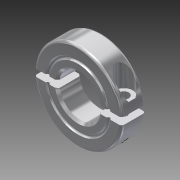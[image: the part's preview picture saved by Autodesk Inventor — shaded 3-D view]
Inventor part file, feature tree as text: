
AUTODESK INVENTOR PART (.ipt)
format: ipt  version: 2016 SP1 (Build 200210100, 210)  size: 259,584 bytes
history: native  units: in
note: dims shown in document units (in); Inventor stores cm internally (conversion verified against a paired STEP export)
features: thread x2, imported_body x2, other x1
ambient origin geometry x8: Origin, YZ Plane, XZ Plane, XY Plane, X Axis, Y Axis, Z Axis, Center Point
bodies: Solid1 (feature_tree), Solid2 (feature_tree)
feature tree (5):
  other  "ENSP20-6-A1"
  thread  "Thread1"  [1 undecoded]
  thread  "Thread2"  [1 undecoded]
  imported_body  "Base1"
  imported_body  "Base2"
note: 2 required parameter values undecoded (feature->parameter linkage not recoverable at this tier; creation-order binding heuristic only, values carry confidence <= 0.55)
